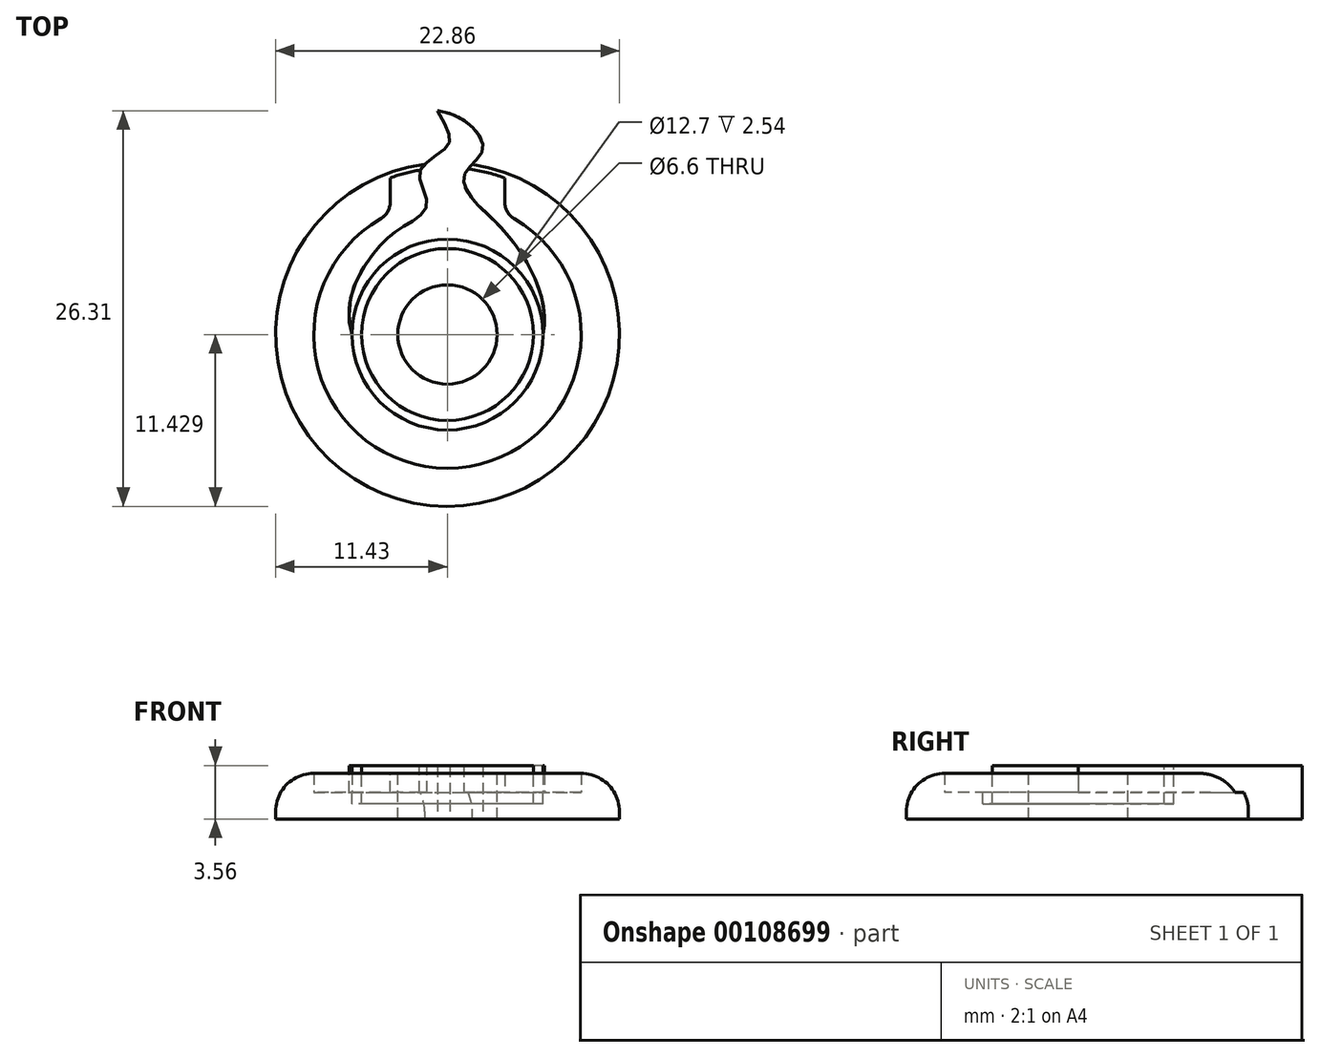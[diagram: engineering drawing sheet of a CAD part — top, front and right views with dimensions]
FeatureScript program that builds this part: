
annotation { "Feature Type Name" : "Feature", "Feature Type Description" : "" }
export const myFeature = defineFeature(function(context is Context, id is Id, definition is map)
    precondition{}
    {
        {
            var Q0;
            Q0=qCreatedBy(makeId("Top.planeOp"),FACE);
            var sketch = newSketch(context, id + "F0", { "sketchPlane" : qUnion([Q0])});
            skCircle(sketch, "E0", {"center": v(0, -2.97) * mm, "radius": 11.43 * mm});
            skSolve(sketch);
        }
        {
            var Q0;
            Q0 = qSketchRegion(id + "F0", true);
            extrude(context, id + "F1", {"entities" : qUnion([Q0]), "depth" : 1.78 * mm});
        }
        {
            var Q0;
            Q0=makeQuery(id+"F1.opExtrude","CAP_FACE",FACE,{"disambiguationData":[OSD([sQuery(id+"F0.wireOp",EDGE,"E0")])],"isStart":false});
            var sketch = newSketch(context, id + "F2", { "sketchPlane" : qUnion([Q0])});
            skCircle(sketch, "E1", {"center": v(0, -2.97) * mm, "radius": 11.43 * mm});
            skCircle(sketch, "E2", {"center": v(0, -2.97) * mm, "radius": 8.9 * mm});
            skLineSegment(sketch, "E3", {"start": v(-3.81, 5.06) * mm, "end": v(-3.81, 7.8) * mm});
            skLineSegment(sketch, "E4", {"start": v(3.81, 5.06) * mm, "end": v(3.81, 7.8) * mm});
            skSolve(sketch);
        }
        {
            var Q0;
            {var subQ0=sQuery(id+"F2.wireOp",EDGE,"E3");Q0=makeQuery(id+"F2.imprint","IMPRINT",FACE,{"disambiguationData":[TD([[makeQuery(id+"F2.imprint","IMPRINT",EDGE,{"derivedFrom":subQ0}),1.0]])]});}
            extrude(context, id + "F3", {"entities" : qUnion([Q0]), "operationType" : NewBodyOperationType.ADD, "depth" : 1.27 * mm});
        }
        {
            var Q0;
            Q0=makeQuery(id+"F1.opExtrude","CAP_FACE",FACE,{"disambiguationData":[OSD([sQuery(id+"F0.wireOp",EDGE,"E0")])],"isStart":false});
            var sketch = newSketch(context, id + "F4", { "sketchPlane" : qUnion([Q0])});
            skCircle(sketch, "E5", {"center": v(0, -2.97) * mm, "radius": 6.35 * mm});
            skCircle(sketch, "E6", {"center": v(0, -2.97) * mm, "radius": 3.27 * mm});
            skFitSpline(sketch, "E7", {"points": [v(-6.35, -2.97) * mm, v(-4.76, 2.61) * mm, v(-2.85, 4.27) * mm, v(-1.36, 5.66) * mm, v(-1.83, 7.88) * mm, v(0, 9.56) * mm, v(-0.68, 11.9) * mm], "startDerivative": vector(-8.74, 29.67) * mm, "endDerivative": vector(-13.06, 22.8) * mm});
            skFitSpline(sketch, "E8", {"points": [v(6.35, -2.97) * mm, v(3.6, 4.1) * mm, v(1.45, 6.32) * mm, v(1.2, 7.8) * mm, v(2.34, 9.32) * mm, v(1.25, 11.16) * mm, v(-0.68, 11.9) * mm], "startDerivative": vector(6.14, 28.64) * mm, "endDerivative": vector(-11.1, 1.23) * mm});
            skSolve(sketch);
        }
        {
            var Q0;
            Q0 = qSketchRegion(id + "F4", true);
            extrude(context, id + "F5", {"entities" : qUnion([Q0]), "operationType" : NewBodyOperationType.ADD, "depth" : 1.78 * mm, "hasSecondDirection" : true, "secondDirectionOppositeDirection" : true, "secondDirectionDepth" : 1.78 * mm});
        }
        {
            var Q0;
            Q0=makeQuery(id+"F5.opExtrude","CAP_FACE",FACE,{"disambiguationData":[OSD([sQuery(id+"F4.wireOp",EDGE,"E5"),sQuery(id+"F4.wireOp",EDGE,"E6"),sQuery(id+"F4.wireOp",EDGE,"E7"),sQuery(id+"F4.wireOp",EDGE,"E8")])],"isStart":false});
            var sketch = newSketch(context, id + "F6", { "sketchPlane" : qUnion([Q0])});
            skCircle(sketch, "E9", {"center": v(0, -2.97) * mm, "radius": 6.35 * mm});
            skCircle(sketch, "E10", {"center": v(0, -2.97) * mm, "radius": 5.72 * mm});
            skSolve(sketch);
        }
        {
            var Q0;
            Q0 = qSketchRegion(id + "F6", true);
            extrude(context, id + "F7", {"entities" : qUnion([Q0]), "operationType" : NewBodyOperationType.REMOVE, "oppositeDirection" : true, "depth" : 2.54 * mm});
        }
        {
            var Q0;
            Q0=makeQuery(id+"F5.boolean.opBoolean","SPLIT",FACE,{"disambiguationData":[TD([makeQuery(id+"F5.opExtrude","SWEPT_FACE",FACE,{"disambiguationData":[OSD([sQuery(id+"F4.wireOp",EDGE,"E6")])]})])],"derivedFrom":makeQuery(id+"F1.opExtrude","CAP_FACE",FACE,{"disambiguationData":[OSD([sQuery(id+"F0.wireOp",EDGE,"E0")])],"isStart":false})});
            var sketch = newSketch(context, id + "F8", { "sketchPlane" : qUnion([Q0])});
            skCircle(sketch, "E11", {"center": v(0, -2.97) * mm, "radius": 3.3 * mm});
            skSolve(sketch);
        }
        {
            var Q0;
            Q0 = qSketchRegion(id + "F8", true);
            extrude(context, id + "F9", {"entities" : qUnion([Q0]), "operationType" : NewBodyOperationType.REMOVE, "oppositeDirection" : true, "depth" : 25.4 * mm, "hasSecondDirection" : true, "secondDirectionOppositeDirection" : false, "secondDirectionDepth" : 25.4 * mm});
        }
        {
            var Q0;
            Q0=makeQuery(id+"F3.opExtrude","CAP_EDGE",EDGE,{"disambiguationData":[OSD([sQuery(id+"F2.wireOp",EDGE,"E1")])],"isStart":false});
            fillet(context, id + "F10", {"entities" : qUnion([Q0]), "radius" : 2.54 * mm, "tangentPropagation" : true, "allowEdgeOverflow" : false});
        }
        {
            var Q0;
            Q0=makeQuery(id+"F3.opExtrude","SWEPT_EDGE",EDGE,{"disambiguationData":[OSD([sQuery(id+"F2.wireOp",EDGE,"E2"),sQuery(id+"F2.wireOp",EDGE,"E3")])]});
            var Q1;
            Q1=makeQuery(id+"F3.opExtrude","SWEPT_EDGE",EDGE,{"disambiguationData":[OSD([sQuery(id+"F2.wireOp",EDGE,"E2"),sQuery(id+"F2.wireOp",EDGE,"E4")])]});
            fillet(context, id + "F11", {"entities" : qUnion([Q0, Q1]), "radius" : 1.27 * mm, "tangentPropagation" : true, "allowEdgeOverflow" : false});
        }
    });
